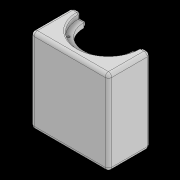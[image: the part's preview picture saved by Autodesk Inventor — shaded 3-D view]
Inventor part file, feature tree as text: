
AUTODESK INVENTOR PART (.ipt)
format: ipt  version: 2022 (Build 260153000, 153)  size: 317,440 bytes
history: native  units: in
note: dims shown in document units (in); Inventor stores cm internally (conversion verified against a paired STEP export)
features: extrude x10, sketch x10, projected_geometry x3, fillet x2, plane x1, split x1, chamfer x1
ambient origin geometry x8: Origin, YZ Plane, XZ Plane, XY Plane, X Axis, Y Axis, Z Axis, Center Point
bodies: Solid1 (feature_tree)
feature tree (28):
  extrude  "Extrusion1"  Depth=4.1339in
  extrude  "Extrusion2"  Depth=2.0669in
  extrude  "Extrusion3"  Depth=0.2756in TaperAngle=0.0deg
  extrude  "Extrusion4"  Depth=0.1969in TaperAngle=0.0deg
  extrude  "Extrusion5"  Depth=0.1969in TaperAngle=0.0deg
  extrude  "Extrusion6"  Depth=0.1969in TaperAngle=0.0deg
  extrude  "Extrusion7"  Depth=0.315in TaperAngle=0.0deg
  extrude  "Extrusion8"  Depth=3.2874in
  plane  "Work Plane1"
  fillet  "Fillet2"  Radius=0.1496in
  fillet  "Fillet3"  Radius=0.1496in
  split  "Split2"
  chamfer  "Chamfer1"  Distance=0.1969in
  extrude  "Extrusion11"  Depth=0.1969in
  extrude  "Extrusion13"  Depth=0.1969in
  sketch  "Sketch1"  dims[d0=4.1339in d1=4.1339in]
  sketch  "Sketch3"  dims[d2=2.0669in d3=2.0669in]
  sketch  "Sketch4"  dims[d4=2.874in d5=0.2756in d6=0.0in]
  sketch  "Sketch6"  dims[d7=4.1339in d8=0.1969in d9=0.0in]
  sketch  "Sketch7"  dims[d10=0.1969in d11=0.0in d12=0.1969in d13=0.0in]
  sketch  "Sketch8"  dims[d14=0.1969in d15=0.0in d16=0.1969in d17=0.0in]
  sketch  "Sketch9"  dims[d18=3.5433in d19=0.315in d20=0.0in]
  projected_geometry  "Projected Loop1"
  sketch  "Sketch10"  dims[d21=0.1496in d22=3.2874in d23=0.1496in d24=0.1496in]
  sketch  "Sketch15"  dims[d25=0.1496in]
  sketch  "Sketch16"  dims[d26=45.0deg d27=0.1969in d28=0.0in d30=0.1969in d31=0.1969in d41=0.0787in d42=0.0787in d43=45.0deg d47=0.1181in d48=0.0in d52=0.0512in d54=0.1575in d55=4.1339in d56=2.0669in d57=0.3937in d58=0.0in d59=0.0591in d33=0.0197in d34=0.0344in d35=0.0197in d36=0.0344in d44=0.0344in d46=0.0197in d49=0.0344in]
  projected_geometry  "Projected Loop3"
  projected_geometry  "Project Cut Edges3"
